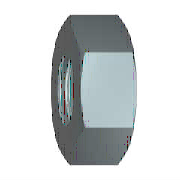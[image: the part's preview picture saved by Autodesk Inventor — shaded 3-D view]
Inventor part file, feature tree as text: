
AUTODESK INVENTOR PART (.ipt)
format: ipt  version: 2024.2 (Build 282272000, 272)  size: 161,792 bytes
history: native  units: mm (DEFAULTED — no unit token found)
features: chamfer x1, hole x1, other x1, plane x1
ambient origin geometry x7: Origin, YZ Plane, XZ Plane, X Axis, Y Axis, Z Axis, Center Point
bodies: Solid1 (feature_tree), Body (feature_tree)
feature tree (4):
  chamfer  "Chamfer1"  Distance=11.547005mm
  hole  "Thread"  [1 undecoded]
  other  "Work Axis1"
  plane  "Work Plane1"
note: 1 required parameter value undecoded (feature->parameter linkage not recoverable at this tier; creation-order binding heuristic only, values carry confidence <= 0.55)
